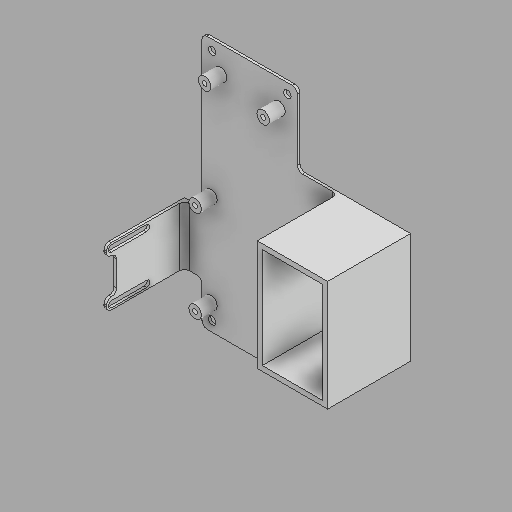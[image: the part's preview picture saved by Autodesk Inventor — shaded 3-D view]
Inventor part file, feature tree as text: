
AUTODESK INVENTOR PART (.ipt)
format: ipt  version: 2025.2 (Build 292293000, 293)  size: 267,264 bytes
history: native  units: in
note: dims shown in document units (in); Inventor stores cm internally (conversion verified against a paired STEP export)
features: sketch x10, extrude x8, hole x2, fillet x1, projected_geometry x1
ambient origin geometry x8: Origin, YZ Plane, XZ Plane, XY Plane, X Axis, Y Axis, Z Axis, Center Point
bodies: Solid1 (feature_tree)
feature tree (22):
  extrude  "Extrusion1"  Depth=2.375in
  extrude  "Extrusion2"  Depth=0.0625in
  hole  "Hole1"  [1 undecoded]
  extrude  "Extrusion3"  Depth=0.3125in
  extrude  "Extrusion4"  Depth=0.3937in TaperAngle=0.0deg
  extrude  "Extrusion5"  Depth=0.25in
  extrude  "Extrusion6"  Depth=0.5in
  extrude  "Extrusion7"  Depth=2.0in TaperAngle=0.0deg
  hole  "Hole2"  [1 undecoded]
  extrude  "Extrusion8"  Depth=0.125in
  fillet  "Fillet2"  Radius=0.1575in
  sketch  "Sketch1"  dims[d0=6.3125in d1=2.375in]
  sketch  "Sketch3"  dims[d2=0.0625in d3=0.0in d4=1.9291in]
  sketch  "Sketch4"  dims[d5=2.2835in d6=1.4567in]
  sketch  "Sketch5"  dims[d7=0.625in d8=0.3125in]
  sketch  "Sketch6"  dims[d9=2.75in d10=0.3937in d11=0.0in]
  sketch  "Sketch7"  dims[d12=5.8125in d13=0.25in]
  sketch  "Sketch8"  dims[d14=0.1875in d15=0.75in d16=0.375in d17=0.25in d18=0.5635in d19=1.0in d20=0.8108in d21=0.5in]
  sketch  "Sketch9"  dims[d22=1.4508in d23=2.0in d24=0.0in]
  projected_geometry  "Projected Loop1"
  sketch  "Sketch10"  dims[d25=1.2008in d26=0.1575in]
  sketch  "Sketch11"  dims[d27=0.875in d28=0.125in d29=0.1575in d30=0.25in d31=0.0in d32=0.0in d33=2.75in d34=2.75in d35=1.0in d36=0.0in d37=1.75in d38=2.0in d39=0.0in d40=0.125in d41=0.125in d42=2.0in d43=0.0in d45=0.1181in d46=0.75in d47=0.375in d48=0.25in d49=0.5635in d50=1.0in d51=0.8108in d52=0.4375in d53=0.0in d54=0.125in]
note: 2 required parameter values undecoded (feature->parameter linkage not recoverable at this tier; creation-order binding heuristic only, values carry confidence <= 0.55)
